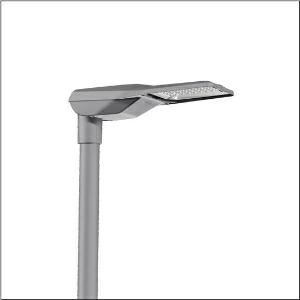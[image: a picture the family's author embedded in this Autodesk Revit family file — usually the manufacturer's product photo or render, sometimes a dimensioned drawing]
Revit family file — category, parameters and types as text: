
# Revit family: streetlight_sl_21_iq_mini___st1_0a_5xe2d41d08hb_6636
name_source: partatom
category: Lighting Fixtures
units: mm (PartAtom-declared; Revit-internal decimal feet)

## family parameters
Cut with Voids When Loaded = No
Host = Face
Light Source = No
Part Type = Normal
Room Calculation Point = No
Round Connector Dimension = Use Diameter
Shared = No

## types (1)
- --- (1 x LED, 9860 lm, 70.9 W, 4000K)
    Apparent Load = 71 VA
    CIE Flux Codes = 37 72 97 100 100
    Color Rendering = 70
    Color Temperature = 4000K
    Default Elevation = 1800 mm
    Description = Streetlight SL 21 iQ mini, mast luminaire, primary light control with lens, of PMMA, primary optical cover: cover, of toughened safety glass, transparent, light distribution: ST1.0a, light emission: direct distribution, primary light characteristic: asymmetric, installation type: post-top, side-entry, LED, High Power LED, rated luminous flux: 9.860lm, luminous efficacy: 139lm/W, light colour: 740, colour temperature: 4000K, control: Auto-Match, Temp-Guard, Lumen-Switch, Night-Set, Smart-Wire, Light-Fading, Desk-Remote (wireless, voltage-free reading and setting of iQ features in the workshop via application-optimized NFC function/RFID function), optimised constant luminous flux control (CLO 2.0), presetting dimming linear, mains connection: 220..240V, AC, 50/60Hz, start of lifetime: 71W, end of service life: 75W, reduction: 31W, luminaire housing, of diecast aluminium, powder-coated, Siteco® metallic grey (DB 702S), corrosivity category C5 mid according to DIN EN ISO 12944, please order mast flange separately, inclination adjustable: 0°, 5°, 10°, 15°, sealing non-destructively replaceable, multi-level sealing system, length: 628mm, width: 235mm, height: 110mm, mast flange for spigot size: 42mm (side-entry): 5XC10008XM4, 60/48mm (side-entry/post-top): 5XC10108XM2, 76/60mm (side-entry/post-top): 5XC10108XM1, protection rating (complete): IP66, insulation class (complete): insulation class II (safety insulation), certification: CE, ENEC, ENEC+, VDE, impact resistance: IK09, permissible operating ambient temperature for outdoor applications: -40..+50°C, standard-compliant lighting for roads and squares, packaging unit: 1 piece

Light Distribution: ST1.0a
    Height = 110 mm
    Lamp = 1 x LED
    Lamp Light Flux = 9860 lm
    Lamp Power = 70.9 W
    Lamp count = 1
    Length = 625 mm
    Luminous efficacy = 139 lm/W
    Manufacturer = Siteco
    ModVariant = No
    Model = 5XE2D41D08HB
    Number of Poles = 1
    OnlyDefault = Yes
    Power Factor = 1
    Product Name = Streetlight SL 21 iQ mini | ST1.0a
    Product group = mast luminaire | pylon top
    ProductGroupID = 6100
    Protection Class = Protection class II
    Protection Degree = IP 66
    RLX_Detail_Level = 1
    RLX_Emergency_Light_Flux = 0 lm
    RLX_Emergency_Type = 0
    RLX_Emergency_Type_DB = No
    RlxData = <blob elided: 91969 chars, md5=aaa30559>
    Socket = socket
    Standby Power = 0 W
    System Light Flux = 9860 lm
    System Power = 71 W
    Type Comments = factory setting: luminous flux: 100 % | dim-lin: 254 | 711 mA
    Type Image = l_1003519.jpg
    URL = http://relux.com
    VarID = @adj_090419
    Voltage = 0 V
    Weight = 0.00 kg
    Width = 234 mm

## geometry (parser evidence)
native form markers: Blend x4, Sweep x10
no freeform markers — native parametric forms only
